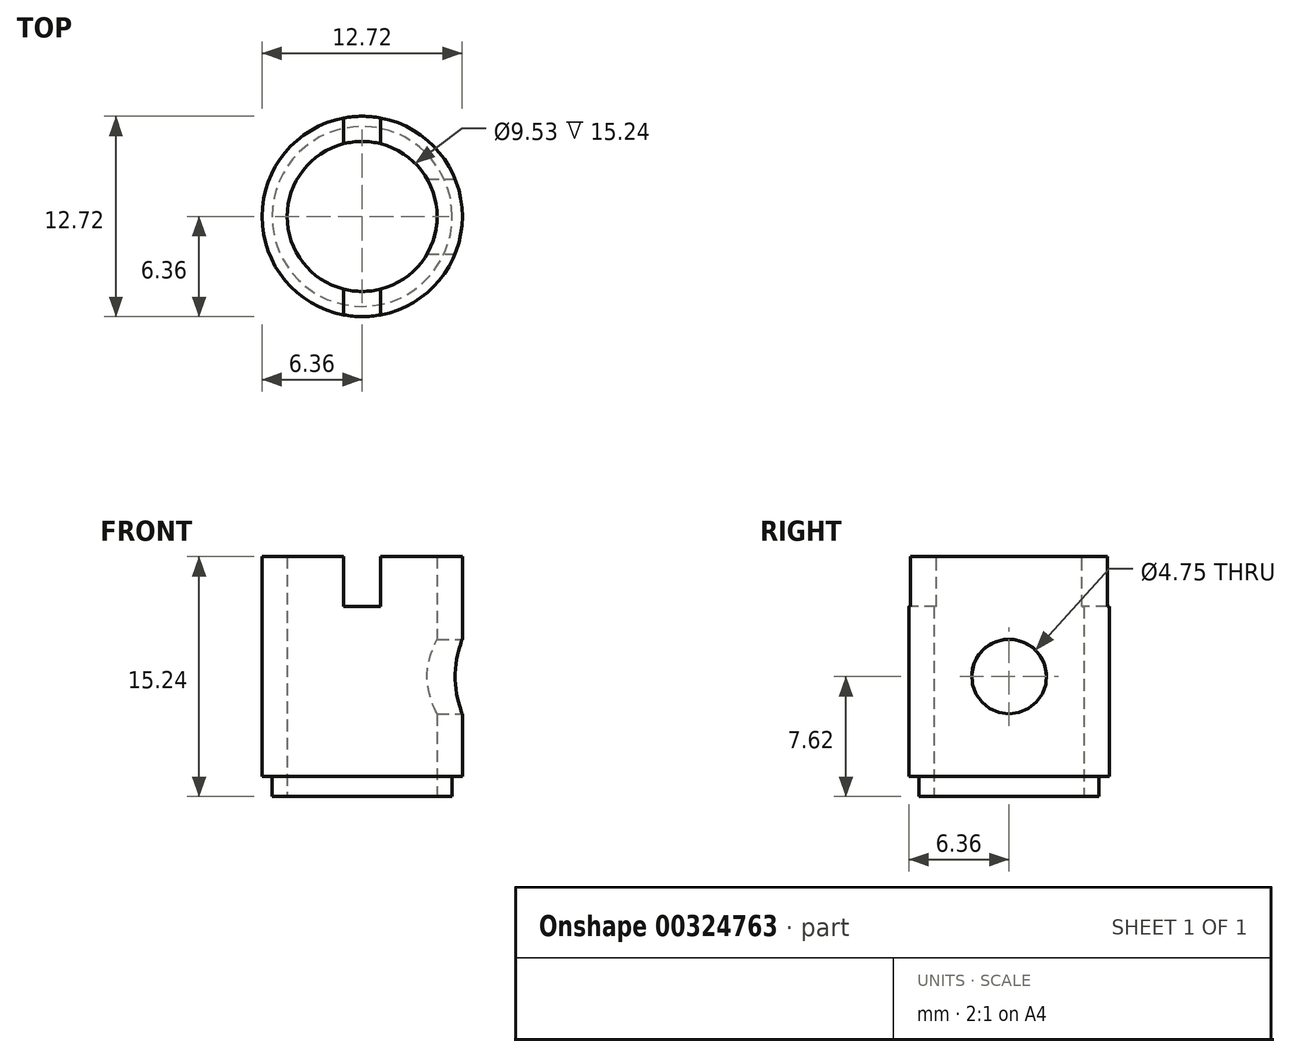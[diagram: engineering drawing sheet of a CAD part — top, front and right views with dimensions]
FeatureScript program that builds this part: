
annotation { "Feature Type Name" : "Feature", "Feature Type Description" : "" }
export const myFeature = defineFeature(function(context is Context, id is Id, definition is map)
    precondition{}
    {
        {
            var Q0;
            Q0=qCreatedBy(makeId("Top.planeOp"),FACE);
            var sketch = newSketch(context, id + "F0", { "sketchPlane" : qUnion([Q0])});
            skCircle(sketch, "E0", {"center": v(0, 0) * mm, "radius": 6.36 * mm});
            skCircle(sketch, "E1", {"center": v(0, 0) * mm, "radius": 4.76 * mm});
            skSolve(sketch);
        }
        {
            var Q0;
            Q0=makeQuery(id+"F0.imprint","IMPRINT",FACE,{"disambiguationData":[TD([[makeQuery(id+"F0.imprint","IMPRINT",EDGE,{"derivedFrom":sQuery(id+"F0.wireOp",EDGE,"E0")}),1.0]])]});
            extrude(context, id + "F1", {"entities" : qUnion([Q0]), "depth" : 15.24 * mm, "offsetDistance" : 25.4 * mm});
        }
        {
            var Q0;
            Q0=makeQuery(id+"F1.opExtrude","CAP_FACE",FACE,{"disambiguationData":[OSD([sQuery(id+"F0.wireOp",EDGE,"E0"),sQuery(id+"F0.wireOp",EDGE,"E1")])],"isStart":true});
            var sketch = newSketch(context, id + "F2", { "sketchPlane" : qUnion([Q0])});
            skCircle(sketch, "E2", {"center": v(0, 0) * mm, "radius": 5.72 * mm});
            skCircle(sketch, "E3", {"center": v(0, 0) * mm, "radius": 6.36 * mm});
            skSolve(sketch);
        }
        {
            var Q0;
            Q0=makeQuery(id+"F2.imprint","IMPRINT",FACE,{"disambiguationData":[TD([[makeQuery(id+"F2.imprint","IMPRINT",EDGE,{"derivedFrom":sQuery(id+"F2.wireOp",EDGE,"E2")}),-1.0]])]});
            extrude(context, id + "F3", {"entities" : qUnion([Q0]), "operationType" : NewBodyOperationType.REMOVE, "oppositeDirection" : true, "depth" : 1.27 * mm, "offsetDistance" : 25.4 * mm});
        }
        {
            var Q0;
            Q0=qCreatedBy(makeId("Right.planeOp"),FACE);
            cPlane(context, id + "F4", {"entities" : qUnion([Q0]), "cplaneType" : CPlaneType.OFFSET, "offset" : 7.94 * mm, "width" : 152.4 * mm, "height" : 152.4 * mm});
        }
        {
            var Q0;
            Q0=qCreatedBy(id+"F4.planeOp",FACE);
            var sketch = newSketch(context, id + "F5", { "sketchPlane" : qUnion([Q0])});
            skArc(sketch, "E4", {"start": v(-2.37, 7.8) * mm, "mid": v(0, 5.25) * mm, "end": v(2.37, 7.8) * mm});
            skArc(sketch, "E5", {"start": v(-2.37, 7.8) * mm, "mid": v(0, 10) * mm, "end": v(2.37, 7.8) * mm});
            skSolve(sketch);
        }
        {
            var Q0;
            Q0=makeQuery(id+"F5.imprint","IMPRINT",FACE,{"disambiguationData":[TD([[makeQuery(id+"F5.imprint","IMPRINT",EDGE,{"derivedFrom":sQuery(id+"F5.wireOp",EDGE,"E4")}),1.0]])]});
            extrude(context, id + "F6", {"entities" : qUnion([Q0]), "operationType" : NewBodyOperationType.REMOVE, "oppositeDirection" : true, "depth" : 5.08 * mm, "offsetDistance" : 25.4 * mm});
        }
        {
            var Q0;
            Q0=makeQuery(id+"F1.opExtrude","CAP_FACE",FACE,{"disambiguationData":[OSD([sQuery(id+"F0.wireOp",EDGE,"E0"),sQuery(id+"F0.wireOp",EDGE,"E1")])],"isStart":false});
            var sketch = newSketch(context, id + "F7", { "sketchPlane" : qUnion([Q0])});
            skLineSegment(sketch, "E6.bottom", {"start": v(-1.18, 7.38) * mm, "end": v(1.18, 7.38) * mm});
            skLineSegment(sketch, "E6.top", {"start": v(-1.18, -6.6) * mm, "end": v(1.18, -6.6) * mm});
            skLineSegment(sketch, "E6.left", {"start": v(-1.18, 7.38) * mm, "end": v(-1.18, -6.6) * mm});
            skLineSegment(sketch, "E6.right", {"start": v(1.18, 7.38) * mm, "end": v(1.18, -6.6) * mm});
            skSolve(sketch);
        }
        {
            var Q0;
            {var subQ0=sQuery(id+"F7.wireOp",EDGE,"E6.left");var subQ1=makeQuery(id+"F1.opExtrude","CAP_EDGE",EDGE,{"disambiguationData":[OSD([sQuery(id+"F0.wireOp",EDGE,"E0")])],"isStart":false});var subQ2=makeQuery(id+"F7.imprint","INTERSECT",VERTEX,{"disambiguationData":[OD(0.0)],"derivedFrom":[subQ1,subQ0]});Q0=makeQuery(id+"F7.imprint","IMPRINT",FACE,{"disambiguationData":[TD([[makeQuery(id+"F7.imprint","IMPRINT",EDGE,{"disambiguationData":[TD([[subQ2,-1.0]])],"derivedFrom":subQ0}),1.0]])]});}
            var Q1;
            {var subQ0=sQuery(id+"F7.wireOp",EDGE,"E6.left");var subQ1=makeQuery(id+"F1.opExtrude","CAP_EDGE",EDGE,{"disambiguationData":[OSD([sQuery(id+"F0.wireOp",EDGE,"E0")])],"isStart":false});var subQ2=makeQuery(id+"F7.imprint","INTERSECT",VERTEX,{"disambiguationData":[OD(1.0)],"derivedFrom":[subQ1,subQ0]});Q1=makeQuery(id+"F7.imprint","IMPRINT",FACE,{"disambiguationData":[TD([[makeQuery(id+"F7.imprint","IMPRINT",EDGE,{"disambiguationData":[TD([[subQ2,1.0]])],"derivedFrom":subQ0}),1.0]])]});}
            extrude(context, id + "F8", {"entities" : qUnion([Q0, Q1]), "operationType" : NewBodyOperationType.REMOVE, "oppositeDirection" : true, "depth" : 3.17 * mm, "offsetDistance" : 25.4 * mm});
        }
    });
